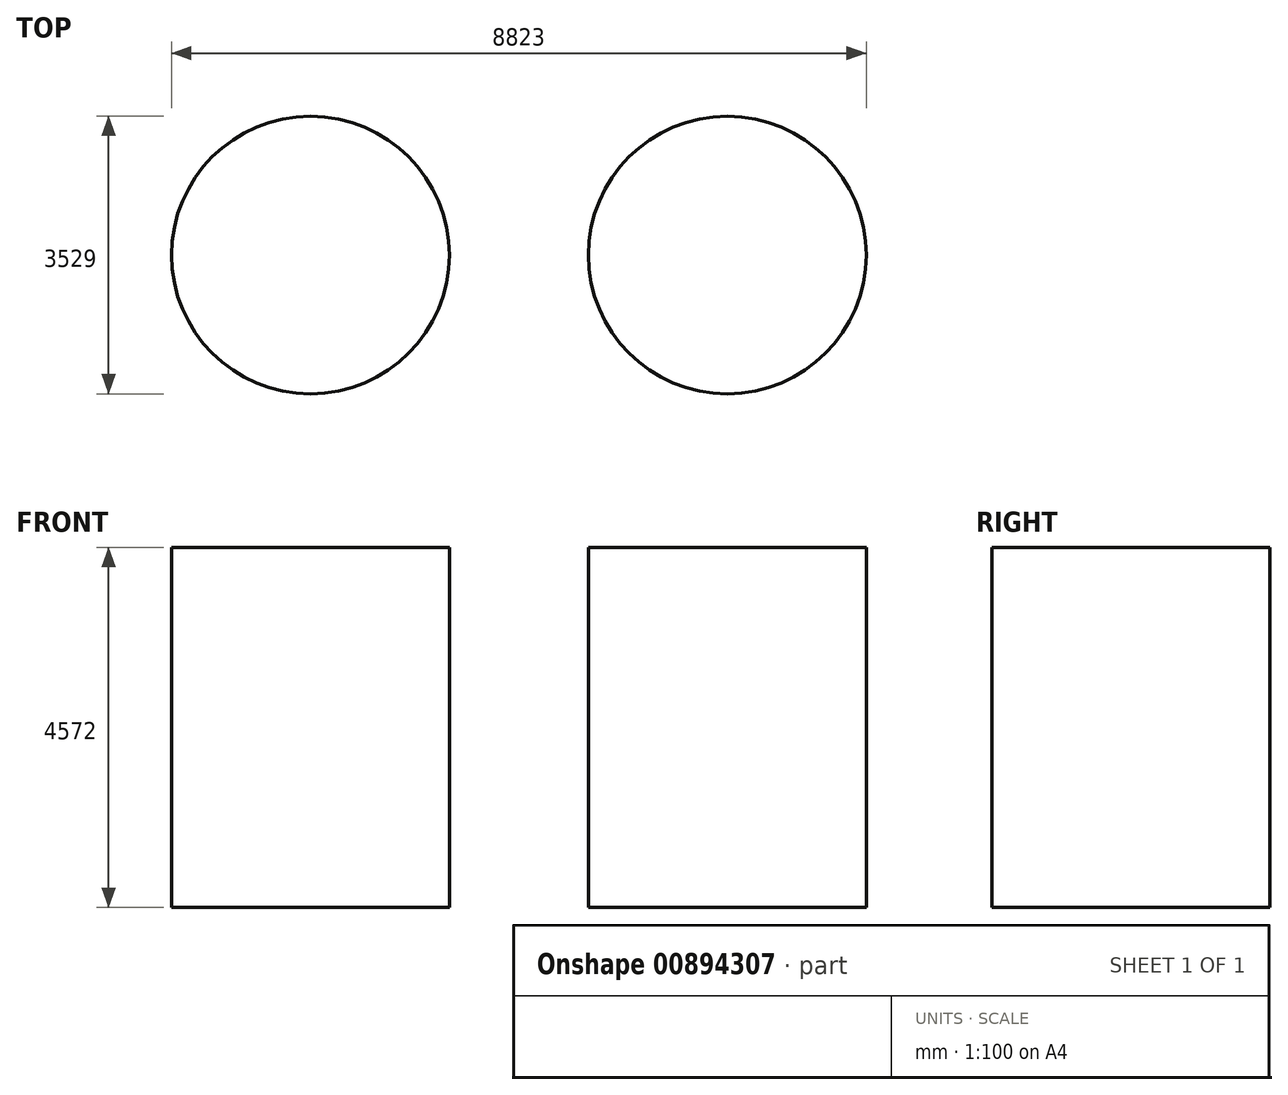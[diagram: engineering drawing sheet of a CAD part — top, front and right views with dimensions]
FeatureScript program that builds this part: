
annotation { "Feature Type Name" : "Feature", "Feature Type Description" : "" }
export const myFeature = defineFeature(function(context is Context, id is Id, definition is map)
    precondition{}
    {
        {
            var Q0;
            Q0=qCreatedBy(makeId("Top.planeOp"),FACE);
            var sketch = newSketch(context, id + "F0", { "sketchPlane" : qUnion([Q0])});
            skCircle(sketch, "E0", {"center": v(0, 0) * mm, "radius": 1764.5 * mm});
            skCircle(sketch, "E1", {"center": v(-5294, 0) * mm, "radius": 1764.5 * mm});
            skSolve(sketch);
        }
        {
            var Q0;
            Q0 = qSketchRegion(id + "F0", true);
            extrude(context, id + "F1", {"entities" : qUnion([Q0]), "depth" : 4572 * mm, "offsetDistance" : 25 * mm});
        }
    });
